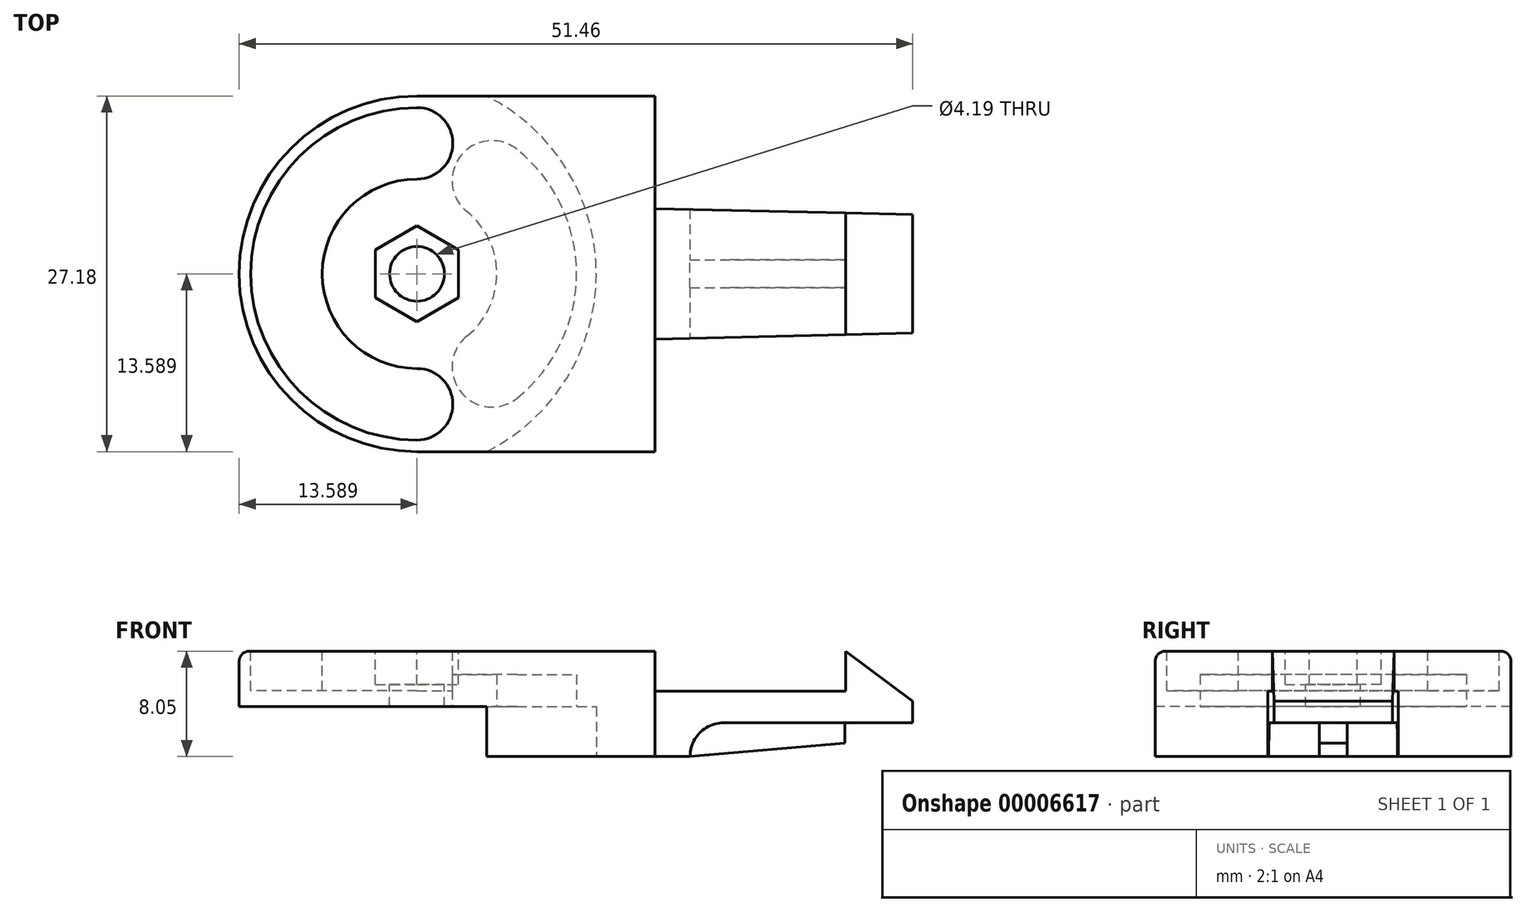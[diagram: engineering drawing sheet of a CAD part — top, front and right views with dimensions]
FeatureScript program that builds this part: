
annotation { "Feature Type Name" : "Feature", "Feature Type Description" : "" }
export const myFeature = defineFeature(function(context is Context, id is Id, definition is map)
    precondition{}
    {
        {
            var Q0;
            Q0=qCreatedBy(makeId("Top.planeOp"),FACE);
            var sketch = newSketch(context, id + "F0", { "sketchPlane" : qUnion([Q0])});
            skLineSegment(sketch, "E0.bottom", {"start": v(13.59, 0) * mm, "end": v(31.78, 0) * mm});
            skLineSegment(sketch, "E0.top", {"start": v(13.59, 27.18) * mm, "end": v(31.78, 27.18) * mm});
            skLineSegment(sketch, "E0.right", {"start": v(51.46, 9.06) * mm, "end": v(51.46, 18.12) * mm});
            skArc(sketch, "E1", {"start": v(13.59, 27.18) * mm, "mid": v(0, 13.59) * mm, "end": v(13.59, 0) * mm});
            skPoint(sketch, "E2.orphan", {"position": v(0, 27.18) * mm});
            skPoint(sketch, "E3.orphan", {"position": v(0, 0) * mm});
            skLineSegment(sketch, "E4", {"start": v(0, 13.59) * mm, "end": v(31.78, 13.59) * mm, "construction": true});
            skLineSegment(sketch, "E5", {"start": v(31.78, 18.57) * mm, "end": v(31.78, 27.18) * mm});
            skLineSegment(sketch, "E6", {"start": v(31.78, 8.6) * mm, "end": v(31.78, 0) * mm});
            skLineSegment(sketch, "E7.0", {"start": v(31.78, 8.6) * mm, "end": v(51.46, 9.06) * mm});
            skLineSegment(sketch, "E8", {"start": v(31.78, 18.57) * mm, "end": v(51.46, 18.12) * mm});
            skPoint(sketch, "E9.start.orphan", {"position": v(51.67, 0) * mm});
            skPoint(sketch, "E10.end.orphan", {"position": v(51.46, 27.18) * mm});
            skSolve(sketch);
        }
        {
            var Q0;
            Q0 = qSketchRegion(id + "F0", true);
            extrude(context, id + "F1", {"entities" : qUnion([Q0]), "depth" : 8.05 * mm});
        }
        {
            var Q0;
            Q0=makeQuery(id+"F1.opExtrude","SWEPT_FACE",FACE,{"disambiguationData":[OSD([sQuery(id+"F0.wireOp",EDGE,"E0.bottom")])]});
            var sketch = newSketch(context, id + "F2", { "sketchPlane" : qUnion([Q0])});
            skLineSegment(sketch, "E11.bottom", {"start": v(31.78, 8.05) * mm, "end": v(46.33, 8.05) * mm});
            skLineSegment(sketch, "E11.top", {"start": v(31.78, 5) * mm, "end": v(46.33, 5) * mm});
            skLineSegment(sketch, "E11.left", {"start": v(31.78, 8.05) * mm, "end": v(31.78, 5) * mm});
            skLineSegment(sketch, "E11.right", {"start": v(46.33, 8.05) * mm, "end": v(46.33, 5) * mm});
            skLineSegment(sketch, "E12.0", {"start": v(31.78, 2.6) * mm, "end": v(51.46, 2.6) * mm});
            skLineSegment(sketch, "E13", {"start": v(46.33, 8.05) * mm, "end": v(51.46, 4.24) * mm});
            skLineSegment(sketch, "E14", {"start": v(45.78, 2.6) * mm, "end": v(45.78, 0) * mm});
            skLineSegment(sketch, "E15", {"start": v(51.46, 4.24) * mm, "end": v(51.46, 2.6) * mm});
            skLineSegment(sketch, "E16", {"start": v(46.33, 8.05) * mm, "end": v(51.46, 8.05) * mm});
            skLineSegment(sketch, "E17", {"start": v(51.46, 8.05) * mm, "end": v(51.46, 0) * mm});
            skLineSegment(sketch, "E18", {"start": v(51.46, 0) * mm, "end": v(31.78, 0) * mm});
            skSolve(sketch);
        }
        {
            var Q0;
            Q0=makeQuery(id+"F2.imprint","IMPRINT",FACE,{"disambiguationData":[TD([[makeQuery(id+"F2.imprint","IMPRINT",EDGE,{"derivedFrom":sQuery(id+"F2.wireOp",EDGE,"E11.bottom")}),-1.0]])]});
            var Q1;
            {var subQ2=sQuery(id+"F2.wireOp",EDGE,"E13");Q1=makeQuery(id+"F2.imprint","IMPRINT",FACE,{"disambiguationData":[TD([[makeQuery(id+"F2.imprint","IMPRINT",EDGE,{"derivedFrom":subQ2}),1.0]])]});}
            var Q2;
            {var subQ3=sQuery(id+"F2.wireOp",EDGE,"E14");Q2=makeQuery(id+"F2.imprint","IMPRINT",FACE,{"disambiguationData":[TD([[makeQuery(id+"F2.imprint","IMPRINT",EDGE,{"derivedFrom":subQ3}),1.0]])]});}
            extrude(context, id + "F3", {"entities" : qUnion([Q0, Q1, Q2]), "operationType" : NewBodyOperationType.REMOVE, "endBound" : BoundingType.THROUGH_ALL, "oppositeDirection" : true, "depth" : 25.4 * mm});
        }
        {
            var Q0;
            Q0=makeQuery(id+"F1.opExtrude","SWEPT_FACE",FACE,{"disambiguationData":[OSD([sQuery(id+"F0.wireOp",EDGE,"E0.bottom")])]});
            var sketch = newSketch(context, id + "F4", { "sketchPlane" : qUnion([Q0])});
            skLineSegment(sketch, "E19", {"start": v(31.78, 0) * mm, "end": v(34.45, 0) * mm});
            skLineSegment(sketch, "E20.bottom", {"start": v(31.78, 0) * mm, "end": v(51.46, 0) * mm});
            skLineSegment(sketch, "E20.top", {"start": v(31.78, 2.6) * mm, "end": v(51.46, 2.6) * mm});
            skLineSegment(sketch, "E20.left", {"start": v(31.78, 0) * mm, "end": v(31.78, 2.6) * mm});
            skLineSegment(sketch, "E20.right", {"start": v(51.46, 0) * mm, "end": v(51.46, 2.6) * mm});
            skLineSegment(sketch, "E21", {"start": v(34.45, 0) * mm, "end": v(37.04, 0) * mm});
            skArc(sketch, "E22", {"start": v(37.04, 2.6) * mm, "mid": v(35.2, 1.83) * mm, "end": v(34.45, 0) * mm});
            skSolve(sketch);
        }
        {
            var Q0;
            {var subQ2=sQuery(id+"F4.wireOp",EDGE,"E20.right");Q0=makeQuery(id+"F4.imprint","IMPRINT",FACE,{"disambiguationData":[TD([[makeQuery(id+"F4.imprint","IMPRINT",EDGE,{"derivedFrom":subQ2}),1.0]])]});}
            extrude(context, id + "F5", {"entities" : qUnion([Q0]), "operationType" : NewBodyOperationType.REMOVE, "endBound" : BoundingType.THROUGH_ALL, "oppositeDirection" : true, "depth" : 11.14 * mm});
        }
        {
            var Q0;
            Q0=makeQuery(id+"F1.opExtrude","CAP_FACE",FACE,{"disambiguationData":[OSD([sQuery(id+"F0.wireOp",EDGE,"E0.bottom"),sQuery(id+"F0.wireOp",EDGE,"E0.top"),sQuery(id+"F0.wireOp",EDGE,"E0.right"),sQuery(id+"F0.wireOp",EDGE,"E1"),sQuery(id+"F0.wireOp",EDGE,"E5"),sQuery(id+"F0.wireOp",EDGE,"E6"),sQuery(id+"F0.wireOp",EDGE,"E7.0"),sQuery(id+"F0.wireOp",EDGE,"E8")])],"isStart":true});
            var sketch = newSketch(context, id + "F6", { "sketchPlane" : qUnion([Q0])});
            skLineSegment(sketch, "E23.0", {"start": v(34.45, -14.66) * mm, "end": v(46.3, -14.66) * mm});
            skLineSegment(sketch, "E24.0", {"start": v(34.45, -12.52) * mm, "end": v(46.3, -12.52) * mm});
            skLineSegment(sketch, "E25", {"start": v(46.3, -12.52) * mm, "end": v(46.3, -14.66) * mm});
            skLineSegment(sketch, "E26", {"start": v(34.45, -14.66) * mm, "end": v(34.45, -12.52) * mm});
            skPoint(sketch, "E27.start.orphan", {"position": v(34.45, -13.59) * mm});
            skSolve(sketch);
        }
        {
            var Q0;
            Q0=makeQuery(id+"F6.imprint","IMPRINT",FACE,{"disambiguationData":[TD([[makeQuery(id+"F6.imprint","IMPRINT",EDGE,{"derivedFrom":sQuery(id+"F6.wireOp",EDGE,"E23.0")}),1.0]])]});
            extrude(context, id + "F7", {"entities" : qUnion([Q0]), "operationType" : NewBodyOperationType.ADD, "endBound" : BoundingType.UP_TO_NEXT, "oppositeDirection" : true, "depth" : 25.4 * mm});
        }
        {
            var Q0;
            Q0=makeQuery(id+"F7.opExtrude","SWEPT_FACE",FACE,{"disambiguationData":[OSD([sQuery(id+"F6.wireOp",EDGE,"E23.0")])]});
            var sketch = newSketch(context, id + "F8", { "sketchPlane" : qUnion([Q0])});
            skLineSegment(sketch, "E28", {"start": v(-46.3, 0) * mm, "end": v(-34.45, 0) * mm});
            skLineSegment(sketch, "E29", {"start": v(-34.45, 0) * mm, "end": v(-46.3, 1.02) * mm});
            skLineSegment(sketch, "E30", {"start": v(-46.3, 1.02) * mm, "end": v(-46.3, 2.6) * mm});
            skLineSegment(sketch, "E31", {"start": v(-46.3, 1.02) * mm, "end": v(-46.3, 0) * mm});
            skSolve(sketch);
        }
        {
            var Q0;
            Q0 = qSketchRegion(id + "F8", true);
            extrude(context, id + "F9", {"entities" : qUnion([Q0]), "operationType" : NewBodyOperationType.REMOVE, "oppositeDirection" : true, "depth" : 25.4 * mm});
        }
        {
            var Q0;
            Q0=makeQuery(id+"F1.opExtrude","CAP_FACE",FACE,{"disambiguationData":[OSD([sQuery(id+"F0.wireOp",EDGE,"E0.bottom"),sQuery(id+"F0.wireOp",EDGE,"E0.top"),sQuery(id+"F0.wireOp",EDGE,"E0.right"),sQuery(id+"F0.wireOp",EDGE,"E1"),sQuery(id+"F0.wireOp",EDGE,"E5"),sQuery(id+"F0.wireOp",EDGE,"E6"),sQuery(id+"F0.wireOp",EDGE,"E7.0"),sQuery(id+"F0.wireOp",EDGE,"E8")])],"isStart":false});
            var sketch = newSketch(context, id + "F10", { "sketchPlane" : qUnion([Q0])});
            skLineSegment(sketch, "E32", {"start": v(0, 13.59) * mm, "end": v(31.78, 13.59) * mm, "construction": true});
            skLineSegment(sketch, "E33", {"start": v(13.59, 27.18) * mm, "end": v(13.59, 0) * mm, "construction": true});
            skCircle(sketch, "E34.cCircle", {"center": v(13.59, 13.59) * mm, "radius": 3.18 * mm, "construction": true});
            skLineSegment(sketch, "E34.0", {"start": v(16.76, 15.42) * mm, "end": v(16.76, 11.76) * mm});
            skLineSegment(sketch, "E34.1", {"start": v(16.76, 11.76) * mm, "end": v(13.59, 9.92) * mm});
            skLineSegment(sketch, "E34.2", {"start": v(13.59, 9.92) * mm, "end": v(10.41, 11.76) * mm});
            skLineSegment(sketch, "E34.3", {"start": v(10.41, 11.76) * mm, "end": v(10.41, 15.42) * mm});
            skLineSegment(sketch, "E34.4", {"start": v(10.41, 15.42) * mm, "end": v(13.59, 17.26) * mm});
            skLineSegment(sketch, "E34.5", {"start": v(13.59, 17.26) * mm, "end": v(16.76, 15.42) * mm});
            skPoint(sketch, "E34.0.midPoint", {"position": v(16.76, 13.59) * mm});
            skSolve(sketch);
        }
        {
            var Q0;
            Q0 = qSketchRegion(id + "F10", true);
            extrude(context, id + "F11", {"entities" : qUnion([Q0]), "operationType" : NewBodyOperationType.REMOVE, "oppositeDirection" : true, "depth" : 2.54 * mm});
        }
        {
            var Q0;
            Q0=makeQuery(id+"F11.boolean.opBoolean","COPY",FACE,{"derivedFrom":makeQuery(id+"F11.opExtrude","CAP_FACE",FACE,{"disambiguationData":[OSD([sQuery(id+"F10.wireOp",EDGE,"E34.0"),sQuery(id+"F10.wireOp",EDGE,"E34.1"),sQuery(id+"F10.wireOp",EDGE,"E34.2"),sQuery(id+"F10.wireOp",EDGE,"E34.3"),sQuery(id+"F10.wireOp",EDGE,"E34.4"),sQuery(id+"F10.wireOp",EDGE,"E34.5")])],"isStart":false})});
            var sketch = newSketch(context, id + "F12", { "sketchPlane" : qUnion([Q0])});
            skLineSegment(sketch, "E35", {"start": v(13.59, 17.26) * mm, "end": v(13.59, 9.92) * mm, "construction": true});
            skLineSegment(sketch, "E36", {"start": v(13.59, 9.92) * mm, "end": v(16.76, 13.59) * mm, "construction": true});
            skLineSegment(sketch, "E37", {"start": v(16.76, 13.59) * mm, "end": v(13.59, 13.59) * mm, "construction": true});
            skCircle(sketch, "E38", {"center": v(13.59, 13.59) * mm, "radius": 2.1 * mm});
            skSolve(sketch);
        }
        {
            var Q0;
            Q0 = qSketchRegion(id + "F12", true);
            extrude(context, id + "F13", {"entities" : qUnion([Q0]), "operationType" : NewBodyOperationType.REMOVE, "endBound" : BoundingType.THROUGH_ALL, "oppositeDirection" : true, "depth" : 25.4 * mm});
        }
        {
            var Q0;
            Q0=makeQuery(id+"F1.opExtrude","CAP_FACE",FACE,{"disambiguationData":[OSD([sQuery(id+"F0.wireOp",EDGE,"E0.bottom"),sQuery(id+"F0.wireOp",EDGE,"E0.top"),sQuery(id+"F0.wireOp",EDGE,"E0.right"),sQuery(id+"F0.wireOp",EDGE,"E1"),sQuery(id+"F0.wireOp",EDGE,"E5"),sQuery(id+"F0.wireOp",EDGE,"E6"),sQuery(id+"F0.wireOp",EDGE,"E7.0"),sQuery(id+"F0.wireOp",EDGE,"E8")])],"isStart":false});
            var sketch = newSketch(context, id + "F14", { "sketchPlane" : qUnion([Q0])});
            skLineSegment(sketch, "E39", {"start": v(13.59, 27.18) * mm, "end": v(13.59, 0) * mm, "construction": true});
            skCircle(sketch, "E40", {"center": v(13.59, 13.59) * mm, "radius": 13.59 * mm, "construction": true});
            skArc(sketch, "E41.2", {"start": v(13.59, 20.83) * mm, "mid": v(6.35, 13.59) * mm, "end": v(13.59, 6.35) * mm});
            skArc(sketch, "E42.trimOffspring", {"start": v(13.59, 26.29) * mm, "mid": v(0.89, 13.59) * mm, "end": v(13.59, 0.89) * mm});
            skArc(sketch, "E43", {"start": v(13.59, 26.29) * mm, "mid": v(16.32, 23.56) * mm, "end": v(13.59, 20.83) * mm});
            skArc(sketch, "E44", {"start": v(13.59, 6.35) * mm, "mid": v(16.32, 3.62) * mm, "end": v(13.59, 0.89) * mm});
            skSolve(sketch);
        }
        {
            var Q0;
            Q0=makeQuery(id+"F14.imprint","IMPRINT",FACE,{"disambiguationData":[TD([[makeQuery(id+"F14.imprint","IMPRINT",EDGE,{"derivedFrom":sQuery(id+"F14.wireOp",EDGE,"E41.2")}),-1.0]])]});
            extrude(context, id + "F15", {"entities" : qUnion([Q0]), "operationType" : NewBodyOperationType.REMOVE, "oppositeDirection" : true, "depth" : 3.02 * mm});
        }
        {
            var Q0;
            Q0=makeQuery(id+"F1.opExtrude","CAP_EDGE",EDGE,{"disambiguationData":[OSD([sQuery(id+"F0.wireOp",EDGE,"E0.bottom")])],"isStart":false});
            var Q1;
            Q1=makeQuery(id+"F3.boolean.opBoolean","MERGE",EDGE,{"derivedFrom":[makeQuery(id+"F1.opExtrude","CAP_EDGE",EDGE,{"disambiguationData":[OSD([sQuery(id+"F0.wireOp",EDGE,"E5")])],"isStart":false}),makeQuery(id+"F1.opExtrude","CAP_EDGE",EDGE,{"disambiguationData":[OSD([sQuery(id+"F0.wireOp",EDGE,"E6")])],"isStart":false})],"fromTools":[makeQuery(id+"F3.opExtrude","SWEPT_EDGE",EDGE,{"disambiguationData":[OSD([sQuery(id+"F0.wireOp",EDGE,"E0.bottom"),sQuery(id+"F2.wireOp",EDGE,"E11.bottom"),sQuery(id+"F2.wireOp",EDGE,"E11.left")])]})]});
            fillet(context, id + "F16", {"entities" : qUnion([Q0, Q1]), "radius" : 0.76 * mm, "tangentPropagation" : true, "allowEdgeOverflow" : false});
        }
        {
            var Q0;
            Q0=makeQuery(id+"F7.boolean.opBoolean","MERGE",FACE,{"derivedFrom":[makeQuery(id+"F1.opExtrude","CAP_FACE",FACE,{"disambiguationData":[OSD([sQuery(id+"F0.wireOp",EDGE,"E0.bottom"),sQuery(id+"F0.wireOp",EDGE,"E0.top"),sQuery(id+"F0.wireOp",EDGE,"E0.right"),sQuery(id+"F0.wireOp",EDGE,"E1"),sQuery(id+"F0.wireOp",EDGE,"E5"),sQuery(id+"F0.wireOp",EDGE,"E6"),sQuery(id+"F0.wireOp",EDGE,"E7.0"),sQuery(id+"F0.wireOp",EDGE,"E8")])],"isStart":true}),makeQuery(id+"F7.opExtrude","CAP_FACE",FACE,{"disambiguationData":[OSD([sQuery(id+"F6.wireOp",EDGE,"E23.0"),sQuery(id+"F6.wireOp",EDGE,"E24.0"),sQuery(id+"F6.wireOp",EDGE,"E25"),sQuery(id+"F6.wireOp",EDGE,"E26")])],"isStart":true})]});
            var sketch = newSketch(context, id + "F17", { "sketchPlane" : qUnion([Q0])});
            skLineSegment(sketch, "E45", {"start": v(31.78, 0) * mm, "end": v(18.91, 0) * mm});
            skLineSegment(sketch, "E46", {"start": v(31.78, -27.18) * mm, "end": v(18.91, -27.18) * mm});
            skArc(sketch, "E47", {"start": v(18.91, -27.18) * mm, "mid": v(27.3, -13.59) * mm, "end": v(18.91, 0) * mm});
            skLineSegment(sketch, "E48", {"start": v(31.78, 0) * mm, "end": v(31.78, -8.6) * mm});
            skLineSegment(sketch, "E49", {"start": v(31.78, -8.6) * mm, "end": v(34.45, -8.67) * mm});
            skLineSegment(sketch, "E50", {"start": v(34.45, -8.67) * mm, "end": v(34.45, -18.51) * mm});
            skLineSegment(sketch, "E51", {"start": v(34.45, -18.51) * mm, "end": v(31.78, -18.57) * mm});
            skLineSegment(sketch, "E52", {"start": v(31.78, -18.57) * mm, "end": v(31.78, -27.18) * mm});
            skSolve(sketch);
        }
        {
            var Q0;
            {var subQ5=sQuery(id+"F17.wireOp",EDGE,"E47");Q0=makeQuery(id+"F17.imprint","IMPRINT",FACE,{"disambiguationData":[TD([[makeQuery(id+"F17.imprint","IMPRINT",EDGE,{"derivedFrom":subQ5}),1.0]])]});}
            extrude(context, id + "F18", {"entities" : qUnion([Q0]), "operationType" : NewBodyOperationType.REMOVE, "oppositeDirection" : true, "depth" : 3.8 * mm});
        }
        {
            var Q0;
            Q0=makeQuery(id+"F18.boolean.opBoolean","COPY",FACE,{"derivedFrom":makeQuery(id+"F18.opExtrude","CAP_FACE",FACE,{"disambiguationData":[OSD([sQuery(id+"F0.wireOp",EDGE,"E0.bottom"),sQuery(id+"F0.wireOp",EDGE,"E0.top"),sQuery(id+"F0.wireOp",EDGE,"E0.right"),sQuery(id+"F0.wireOp",EDGE,"E1"),sQuery(id+"F0.wireOp",EDGE,"E5"),sQuery(id+"F0.wireOp",EDGE,"E6"),sQuery(id+"F0.wireOp",EDGE,"E7.0"),sQuery(id+"F0.wireOp",EDGE,"E8"),sQuery(id+"F6.wireOp",EDGE,"E23.0"),sQuery(id+"F6.wireOp",EDGE,"E24.0"),sQuery(id+"F6.wireOp",EDGE,"E25"),sQuery(id+"F6.wireOp",EDGE,"E26"),sQuery(id+"F12.wireOp",EDGE,"E38"),sQuery(id+"F17.wireOp",EDGE,"E47")])],"isStart":false})});
            var sketch = newSketch(context, id + "F19", { "sketchPlane" : qUnion([Q0])});
            skArc(sketch, "E53", {"start": v(21.23, -23.1) * mm, "mid": v(25.78, -13.59) * mm, "end": v(21.23, -4.09) * mm});
            skArc(sketch, "E54.0", {"start": v(17.4, -18.34) * mm, "mid": v(19.69, -13.59) * mm, "end": v(17.4, -8.84) * mm});
            skPoint(sketch, "E55.end.orphan", {"position": v(25.78, -13.59) * mm});
            skPoint(sketch, "E56.start.orphan", {"position": v(19.69, -13.59) * mm});
            skArc(sketch, "E57", {"start": v(17.4, -8.84) * mm, "mid": v(16.94, -4.55) * mm, "end": v(21.23, -4.09) * mm});
            skArc(sketch, "E58", {"start": v(17.4, -18.34) * mm, "mid": v(16.94, -22.63) * mm, "end": v(21.23, -23.1) * mm});
            skSolve(sketch);
        }
        {
            var Q0;
            Q0=makeQuery(id+"F19.imprint","IMPRINT",FACE,{"disambiguationData":[TD([[makeQuery(id+"F19.imprint","IMPRINT",EDGE,{"derivedFrom":sQuery(id+"F19.wireOp",EDGE,"E53")}),1.0]])]});
            extrude(context, id + "F20", {"entities" : qUnion([Q0]), "operationType" : NewBodyOperationType.REMOVE, "oppositeDirection" : true, "depth" : 2.45 * mm});
        }
    });
